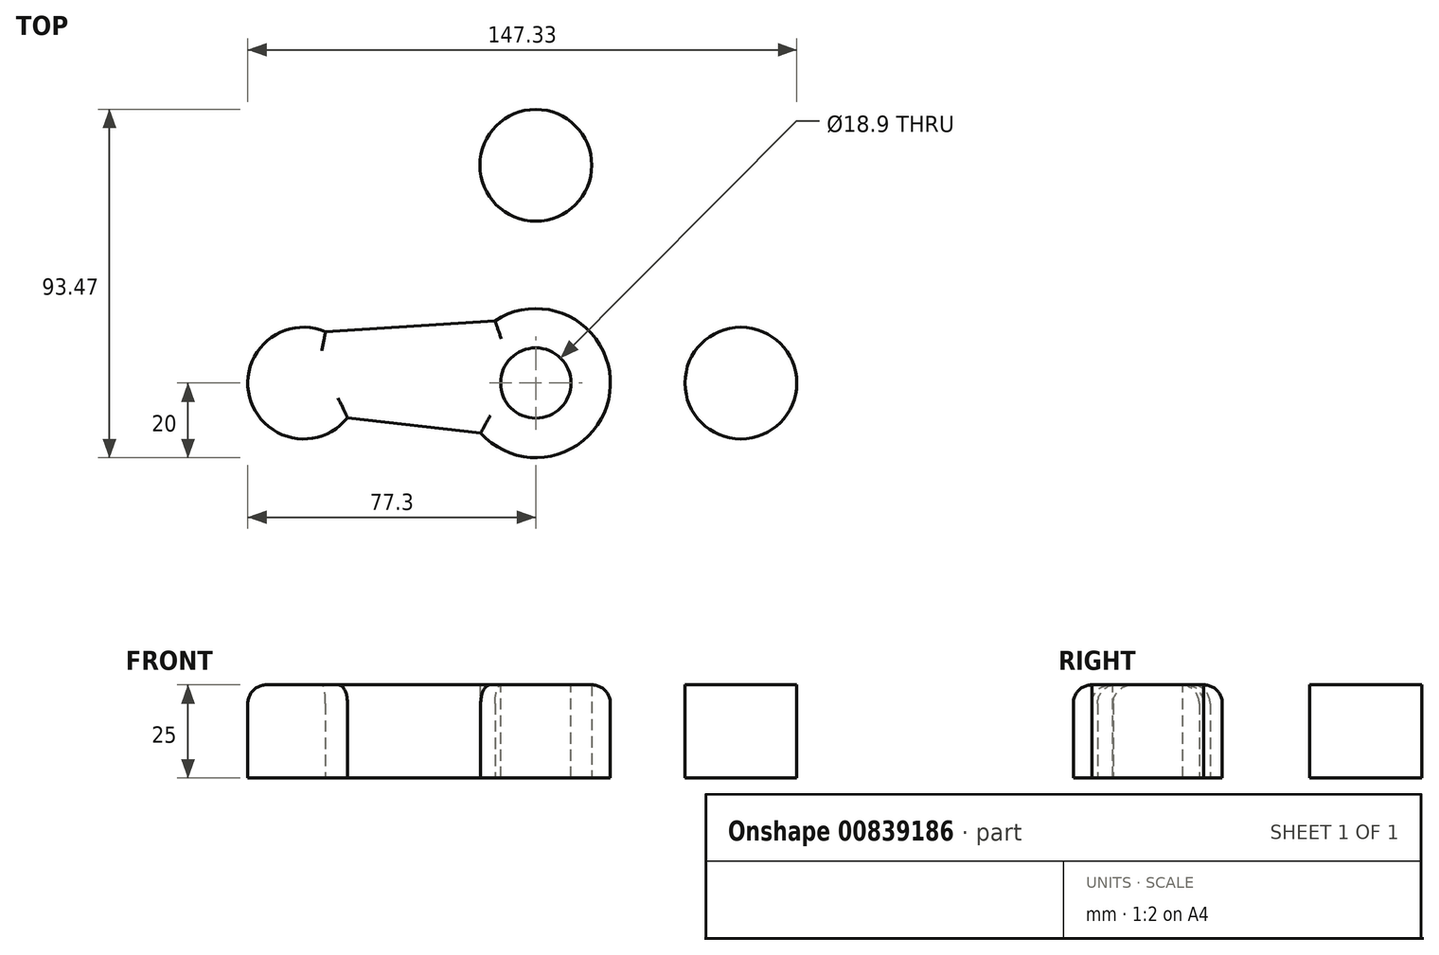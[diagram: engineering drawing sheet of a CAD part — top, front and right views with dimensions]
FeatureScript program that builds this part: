
annotation { "Feature Type Name" : "Feature", "Feature Type Description" : "" }
export const myFeature = defineFeature(function(context is Context, id is Id, definition is map)
    precondition{}
    {
        {
            var Q0;
            Q0=qCreatedBy(makeId("Top.planeOp"),FACE);
            var sketch = newSketch(context, id + "F0", { "sketchPlane" : qUnion([Q0])});
            skCircle(sketch, "E0", {"center": v(0, 0) * mm, "radius": 20 * mm});
            skCircle(sketch, "E1", {"center": v(0, 58.47) * mm, "radius": 15 * mm});
            skCircle(sketch, "E2", {"center": v(55.03, 0) * mm, "radius": 15 * mm});
            skCircle(sketch, "E3", {"center": v(-62.3, 0) * mm, "radius": 15 * mm});
            skLineSegment(sketch, "E4", {"start": v(-56.45, 13.81) * mm, "end": v(-10.96, 16.73) * mm});
            skLineSegment(sketch, "E5", {"start": v(-50.56, -9.33) * mm, "end": v(-14.8, -13.46) * mm});
            skSolve(sketch);
        }
        {
            var Q0;
            Q0 = qSketchRegion(id + "F0", true);
            extrude(context, id + "F1", {"entities" : qUnion([Q0]), "depth" : 25 * mm, "offsetDistance" : 25 * mm});
        }
        {
            var Q0;
            Q0=makeQuery(id+"F1.opExtrude","CAP_EDGE",EDGE,{"disambiguationData":[OSD([sQuery(id+"F0.wireOp",EDGE,"E5")])],"isStart":false});
            var Q1;
            Q1=makeQuery(id+"F1.opExtrude","CAP_EDGE",EDGE,{"disambiguationData":[OSD([sQuery(id+"F0.wireOp",EDGE,"E3")])],"isStart":false});
            var Q2;
            Q2=makeQuery(id+"F1.opExtrude","CAP_EDGE",EDGE,{"disambiguationData":[OSD([sQuery(id+"F0.wireOp",EDGE,"E0")])],"isStart":false});
            var Q3;
            Q3=makeQuery(id+"F1.opExtrude","CAP_EDGE",EDGE,{"disambiguationData":[OSD([sQuery(id+"F0.wireOp",EDGE,"E4")])],"isStart":false});
            fillet(context, id + "F2", {"entities" : qUnion([Q0, Q1, Q2, Q3]), "radius" : 5 * mm, "tangentPropagation" : true, "allowEdgeOverflow" : false});
        }
        {
            var Q0;
            Q0=makeQuery(id+"F1.opExtrude","CAP_FACE",FACE,{"disambiguationData":[OSD([sQuery(id+"F0.wireOp",EDGE,"E0"),sQuery(id+"F0.wireOp",EDGE,"E3"),sQuery(id+"F0.wireOp",EDGE,"E4"),sQuery(id+"F0.wireOp",EDGE,"E5")])],"isStart":false});
            var sketch = newSketch(context, id + "F3", { "sketchPlane" : qUnion([Q0])});
            skCircle(sketch, "E6", {"center": v(0, 0) * mm, "radius": 9.45 * mm});
            skSolve(sketch);
        }
        {
            var Q0;
            Q0 = qSketchRegion(id + "F3", true);
            extrude(context, id + "F4", {"entities" : qUnion([Q0]), "operationType" : NewBodyOperationType.REMOVE, "oppositeDirection" : true, "depth" : 25 * mm, "offsetDistance" : 25 * mm});
        }
    });
